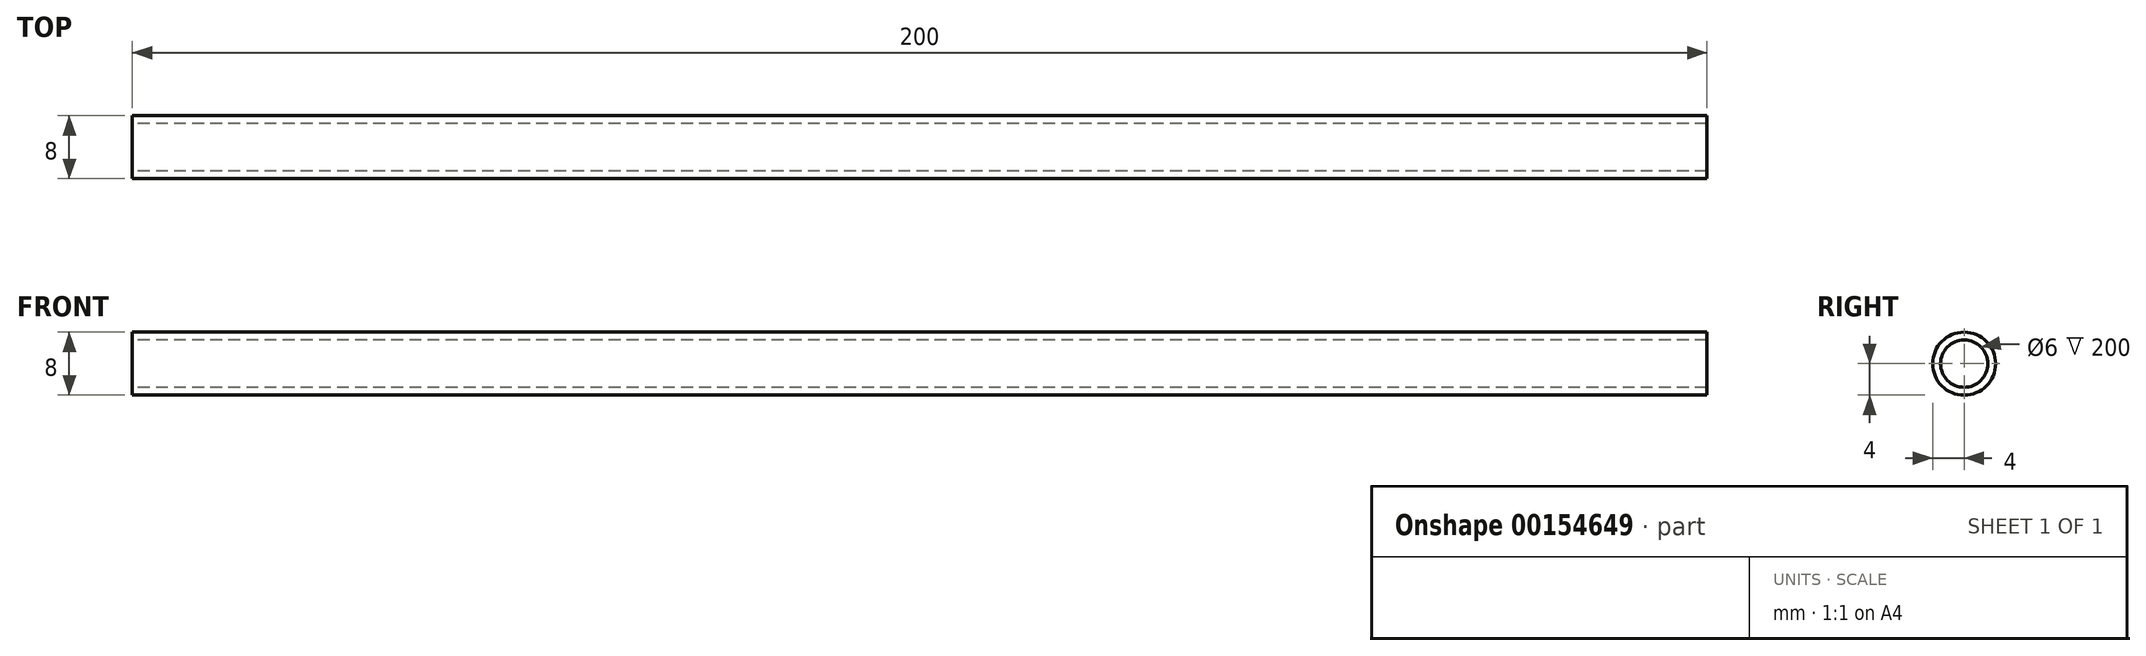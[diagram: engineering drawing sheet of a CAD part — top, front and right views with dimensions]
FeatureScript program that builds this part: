
annotation { "Feature Type Name" : "Feature", "Feature Type Description" : "" }
export const myFeature = defineFeature(function(context is Context, id is Id, definition is map)
    precondition{}
    {
        {
            var Q0;
            Q0=qCreatedBy(makeId("Right.planeOp"),FACE);
            var sketch = newSketch(context, id + "F0", { "sketchPlane" : qUnion([Q0])});
            skCircle(sketch, "E0", {"center": v(0, 0) * mm, "radius": 4 * mm});
            skCircle(sketch, "E1", {"center": v(0, 0) * mm, "radius": 3 * mm});
            skSolve(sketch);
        }
        {
            var Q0;
            Q0 = qSketchRegion(id + "F0", true);
            extrude(context, id + "F1", {"entities" : qUnion([Q0]), "depth" : 200 * mm});
        }
    });
